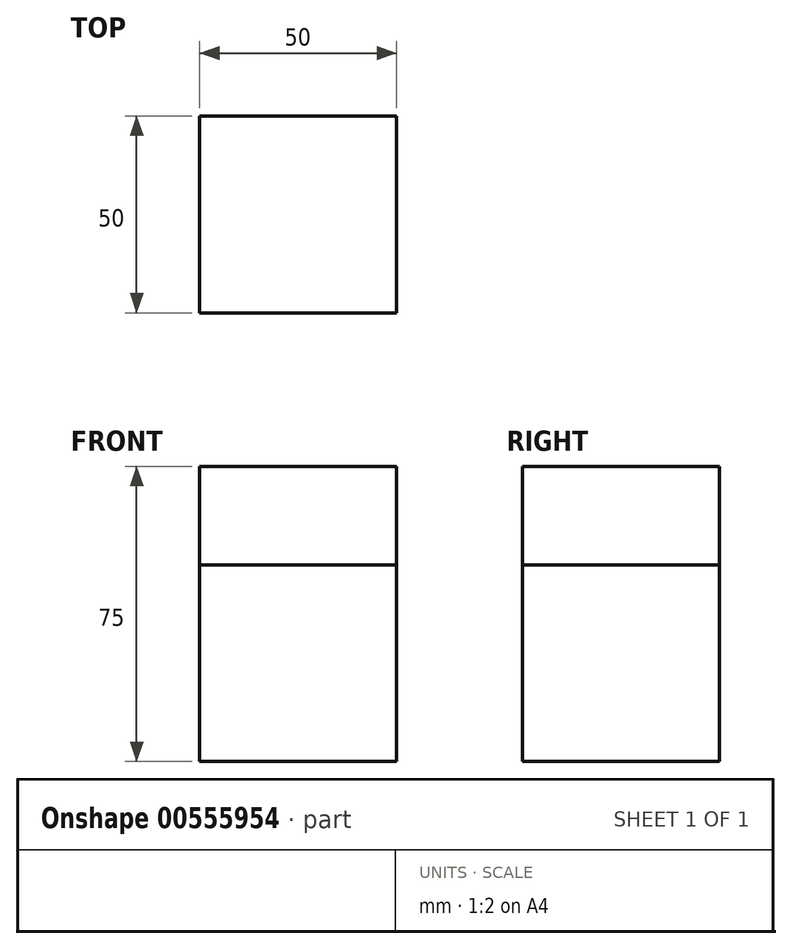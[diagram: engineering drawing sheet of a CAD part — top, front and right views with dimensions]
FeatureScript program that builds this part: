
annotation { "Feature Type Name" : "Feature", "Feature Type Description" : "" }
export const myFeature = defineFeature(function(context is Context, id is Id, definition is map)
    precondition{}
    {
        {
            var Q0;
            Q0=qCreatedBy(makeId("Top.planeOp"),FACE);
            var sketch = newSketch(context, id + "F0", { "sketchPlane" : qUnion([Q0])});
            skLineSegment(sketch, "E0.bottom", {"start": v(-50, 0) * mm, "end": v(0, 0) * mm});
            skLineSegment(sketch, "E0.top", {"start": v(-50, 50) * mm, "end": v(0, 50) * mm});
            skLineSegment(sketch, "E0.left", {"start": v(-50, 0) * mm, "end": v(-50, 50) * mm});
            skLineSegment(sketch, "E0.right", {"start": v(0, 0) * mm, "end": v(0, 50) * mm});
            skSolve(sketch);
        }
        {
            var Q0;
            Q0=makeQuery(id+"F0.imprint","IMPRINT",FACE,{"disambiguationData":[TD([[makeQuery(id+"F0.imprint","IMPRINT",EDGE,{"derivedFrom":sQuery(id+"F0.wireOp",EDGE,"E0.bottom")}),1.0]])]});
            extrude(context, id + "F1", {"entities" : qUnion([Q0]), "oppositeDirection" : true, "depth" : 50 * mm, "offsetDistance" : 25 * mm});
        }
        {
            var Q0;
            Q0=makeQuery(id+"F1.opExtrude","CAP_FACE",FACE,{"disambiguationData":[OSD([sQuery(id+"F0.wireOp",EDGE,"E0.bottom"),sQuery(id+"F0.wireOp",EDGE,"E0.top"),sQuery(id+"F0.wireOp",EDGE,"E0.left"),sQuery(id+"F0.wireOp",EDGE,"E0.right")])],"isStart":true});
            var sketch = newSketch(context, id + "F2", { "sketchPlane" : qUnion([Q0])});
            skLineSegment(sketch, "E1.bottom", {"start": v(-50, 0) * mm, "end": v(0, 0) * mm});
            skLineSegment(sketch, "E1.top", {"start": v(-50, 50) * mm, "end": v(0, 50) * mm});
            skLineSegment(sketch, "E1.left", {"start": v(-50, 0) * mm, "end": v(-50, 50) * mm});
            skLineSegment(sketch, "E1.right", {"start": v(0, 0) * mm, "end": v(0, 50) * mm});
            skSolve(sketch);
        }
        {
            var Q0;
            Q0=makeQuery(id+"F2.imprint","IMPRINT",FACE,{"disambiguationData":[TD([[makeQuery(id+"F2.imprint","IMPRINT",EDGE,{"derivedFrom":sQuery(id+"F2.wireOp",EDGE,"E1.bottom")}),1.0]])]});
            extrude(context, id + "F3", {"entities" : qUnion([Q0]), "depth" : 25 * mm, "offsetDistance" : 25 * mm});
        }
    });
